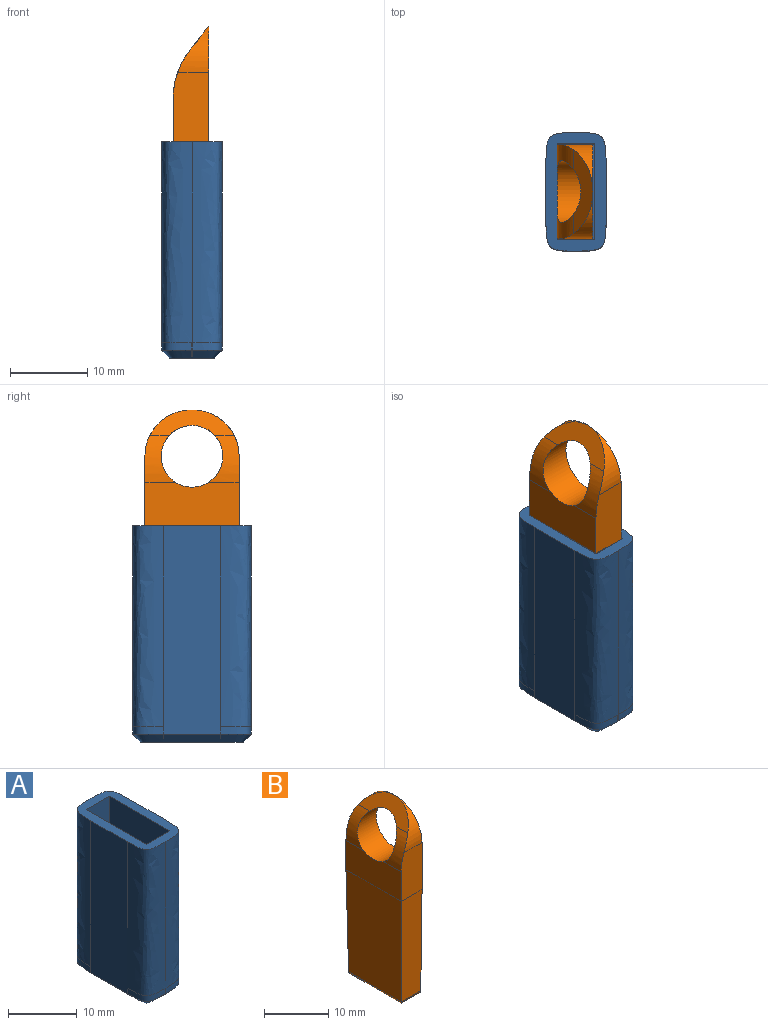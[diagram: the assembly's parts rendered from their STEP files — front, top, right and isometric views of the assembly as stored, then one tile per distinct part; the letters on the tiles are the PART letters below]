
ASSEMBLY  parts=2 mates=1
PART A: 27 faces, bbox 9.3x16.9x30.8 mm
  f0: plane 26x12.4mm, normal (-1,0,0), area 322.4mm2, adj f1,f5,f6,f11
  f1: plane 26x4.8mm, normal (0,1,0), area 124.8mm2, adj f0,f2,f6,f11
  f2: plane 26x12.4mm, normal (1,0,0), area 322.4mm2, adj f1,f5,f6,f11
  f3: plane 27x7.4mm, normal (1,0,0), area 199.8mm2, adj f6,f7,f10,f15,f16,f26
  f4: plane 27x7.4mm, normal (-1,0,0), area 199.8mm2, adj f6,f8,f9,f12,f13,f19
  f5: plane 26x4.8mm, normal (0,-1,0), area 124.8mm2, adj f0,f2,f6,f11
  f6: plane 16.91x9.31mm, normal (0,0,1), area 56.4mm2, adj f0,f1,f2,f3,f4,f5,f7,f8
  f7: bspline ~28.6x4mm, area 179.3mm2, adj f3,f6,f8,f16
  f8: bspline ~28.6x4mm, area 181.9mm2, adj f4,f6,f7,f12,f17
  f9: bspline ~28.6x4mm, area 179.3mm2, adj f4,f6,f10,f13
  f10: bspline ~28.6x4mm, area 181.9mm2, adj f3,f6,f9,f14,f15
  f11: plane 12.4x4.8mm, normal (0,0,1), area 59.5mm2, adj f0,f1,f2,f5
  f12: bspline ~4x3.8mm, area 6.8mm2, adj f4,f8,f17,f21
  f13: bspline ~4x3.8mm, area 6.8mm2, adj f4,f9,f14,f20
  f14: bspline ~2x0.2mm, area 0.2mm2, adj f10,f13,f15,f22
  f15: bspline ~4x3.8mm, area 6.8mm2, adj f3,f10,f14,f24
  f16: bspline ~4x3.8mm, area 6.8mm2, adj f3,f7,f17,f25
  f17: bspline ~2x0.2mm, area 0.2mm2, adj f8,f12,f16,f23
  f18: plane 14.41x6.81mm, normal (0,0,-1), area 76mm2, adj f19,f20,f21,f22,f23,f24,f25,f26
  f19: plane 7.4x1mm, normal (-0.71,0,-0.71), area 10.5mm2, adj f4,f18,f20,f21
  f20: bspline ~4.01x3.82mm, area 8.4mm2, adj f13,f18,f19,f22
  f21: bspline ~4.01x3.82mm, area 8.5mm2, adj f12,f18,f19,f23
  f22: bspline ~1.01x1.01mm, area 0.3mm2, adj f14,f18,f20,f24
  f23: bspline ~1.01x1.01mm, area 0.3mm2, adj f17,f18,f21,f25
  f24: bspline ~4x3.81mm, area 8.5mm2, adj f15,f18,f22,f26
  f25: bspline ~4x3.81mm, area 8.4mm2, adj f16,f18,f23,f26
  f26: plane 7.4x1mm, normal (0.71,0,-0.71), area 10.5mm2, adj f3,f18,f24,f25
PART B: 18 faces, bbox 4.6x12.2x35 mm
  f0: plane 12.2x5.61mm, normal (-1,0,0), area 66.7mm2, adj f3,f5,f8,f9,f10,f12
  f1: cylinder r=6mm len=6mm, axis (1,0,0), area 15.2mm2, adj f3,f4,f7,f10
  f2: cylinder r=6mm len=6mm, axis (-1,0,0), area 15.2mm2, adj f4,f5,f7,f9
  f3: plane 9x4.6mm, normal (0,-1,0), area 40.7mm2, adj f0,f1,f4,f10,f13
  f4: plane 34.5x12.2mm, normal (1,0,0), area 349.5mm2, adj f1,f2,f3,f5,f7,f8,f11,f13
  f5: plane 9x4.6mm, normal (0,1,0), area 40.7mm2, adj f0,f2,f4,f9,f11
  f6: plane 10.62x3.31mm, normal (0,0,-1), area 35.1mm2, adj f14,f15,f16,f17
  f7: plane 10.92x3.31mm, normal (-0.79,0,0.61), area 26mm2, adj f1,f2,f4,f8,f9,f10
  f8: cylinder r=4mm len=8mm, axis (-1,0,0), area 88.6mm2, adj f0,f4,f7,f9,f10
  f9: cylinder r=10mm len=6.08mm, axis (0,1,0), area 16mm2, adj f0,f2,f5,f7,f8
  f10: cylinder r=10mm len=6.08mm, axis (0,1,0), area 16mm2, adj f0,f1,f3,f7,f8
  f11: plane 19.51x4.6mm, normal (0,1,-0.01), area 86.9mm2, adj f4,f5,f12,f14,f15
  f12: plane 19.51x12.2mm, normal (-1,0,-0.01), area 232.3mm2, adj f0,f11,f13,f16
  f13: plane 19.51x4.6mm, normal (0,-1,-0.01), area 86.9mm2, adj f3,f4,f12,f15,f17
  f14: cylinder r=0.5mm len=4.31mm, axis (1,0,0), area 3.1mm2, adj f6,f11,f15,f16
  f15: cylinder r=0.5mm len=11.62mm, axis (0,-1,0), area 8.8mm2, adj f4,f6,f11,f13,f14,f17
  f16: cylinder r=0.5mm len=11.61mm, axis (0,-1,0), area 8.7mm2, adj f6,f12,f14,f17
  f17: cylinder r=0.5mm len=4.31mm, axis (1,0,0), area 3.1mm2, adj f6,f13,f15,f16
PLACE A t=(11.82,3.97,-59.28)mm fixed
PLACE B t=(11.67,3.97,-79.28)mm
MATE slider B.f6 <-> A.f11  axis (0,0,-1) through (14.22,-2.23,-53.28)mm
